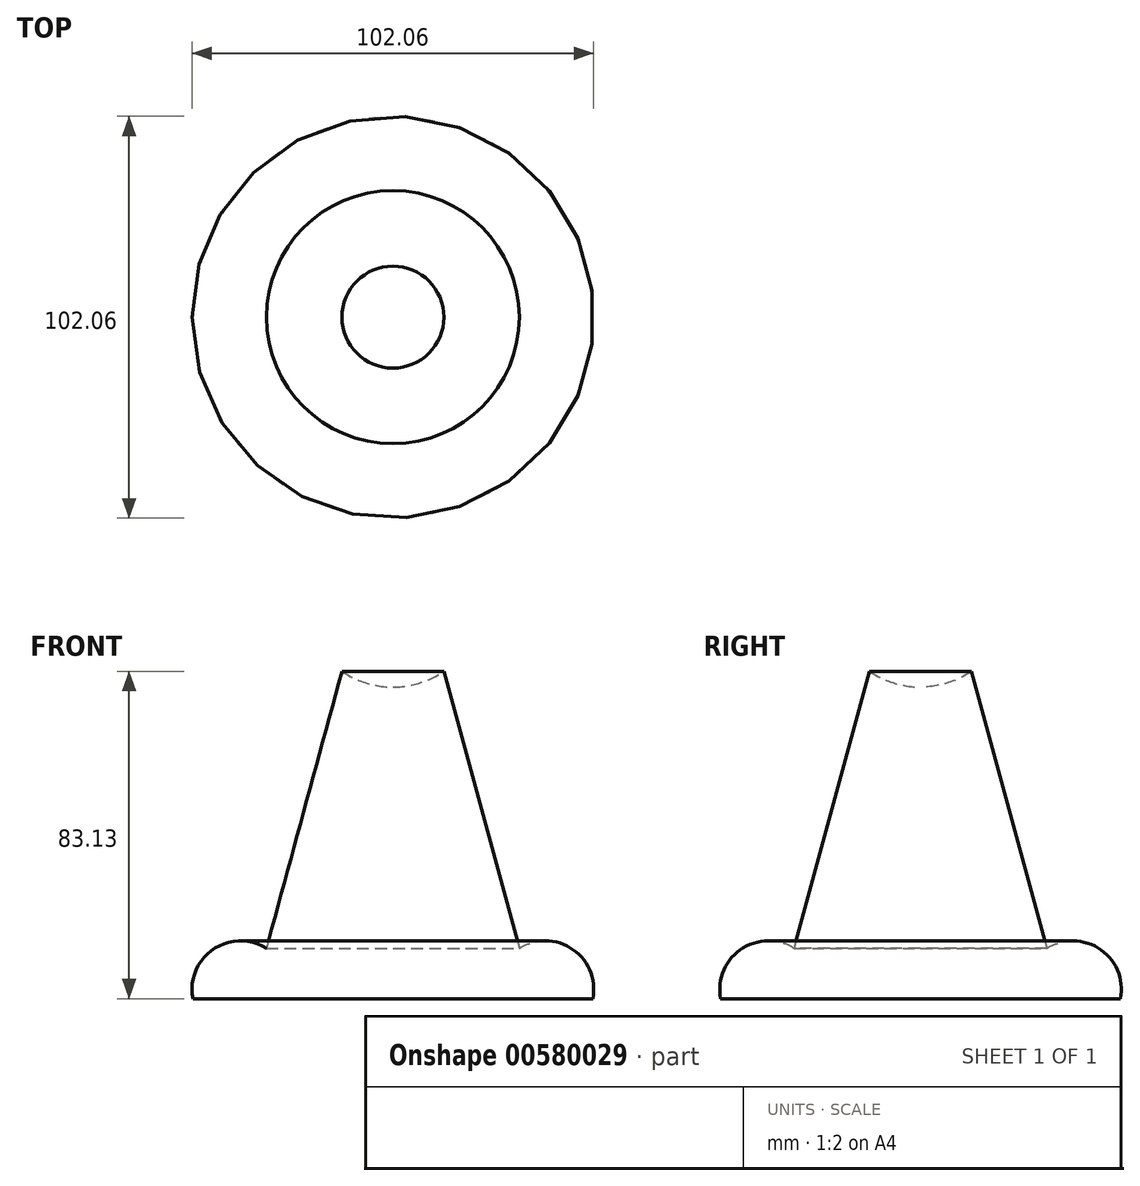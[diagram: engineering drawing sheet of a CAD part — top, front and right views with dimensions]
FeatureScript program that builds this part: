
annotation { "Feature Type Name" : "Feature", "Feature Type Description" : "" }
export const myFeature = defineFeature(function(context is Context, id is Id, definition is map)
    precondition{}
    {
        {
            var Q0;
            Q0=qCreatedBy(makeId("Front.planeOp"),FACE);
            var sketch = newSketch(context, id + "F0", { "sketchPlane" : qUnion([Q0])});
            skLineSegment(sketch, "E0", {"start": v(0, 0) * mm, "end": v(0, 127) * mm});
            skLineSegment(sketch, "E1", {"start": v(0, 0) * mm, "end": v(50.8, 0) * mm});
            skArc(sketch, "E2", {"start": v(50.8, 0) * mm, "mid": v(45.67, 12.54) * mm, "end": v(32.13, 12.8) * mm});
            skLineSegment(sketch, "E3", {"start": v(32.13, 12.8) * mm, "end": v(12.95, 83.13) * mm});
            skArc(sketch, "E4", {"start": v(0, 79.17) * mm, "mid": v(23.69, 103.09) * mm, "end": v(0, 127) * mm});
            skLineSegment(sketch, "E5", {"start": v(32.13, 12.8) * mm, "end": v(0, 12.8) * mm});
            skSolve(sketch);
        }
        {
            var Q0;
            {var subQ0=sQuery(id+"F0.wireOp",EDGE,"E1");Q0=makeQuery(id+"F0.imprint","IMPRINT",FACE,{"disambiguationData":[TD([[makeQuery(id+"F0.imprint","IMPRINT",EDGE,{"derivedFrom":subQ0}),1.0]])]});}
            var Q1;
            {var subQ3=sQuery(id+"F0.wireOp",EDGE,"E5");Q1=makeQuery(id+"F0.imprint","IMPRINT",FACE,{"disambiguationData":[TD([[makeQuery(id+"F0.imprint","IMPRINT",EDGE,{"derivedFrom":subQ3}),-1.0]])]});}
            var Q2;
            {var subQ0=sQuery(id+"F0.wireOp",EDGE,"E4");var subQ1=sQuery(id+"F0.wireOp",EDGE,"E0");var subQ2=makeQuery(id+"F0.imprint","INTERSECT",VERTEX,{"disambiguationData":[OD(0.0)],"derivedFrom":[subQ1,subQ0]});Q2=makeQuery(id+"F0.imprint","IMPRINT",FACE,{"disambiguationData":[TD([[makeQuery(id+"F0.imprint","IMPRINT",EDGE,{"disambiguationData":[TD([[subQ2,1.0]])],"derivedFrom":subQ1}),-1.0]])]});}
            var Q3;
            Q3=sQuery(id+"F0.wireOp",EDGE,"E0");
            revolve(context, id + "F1", {"entities" : qUnion([Q0, Q1, Q2]), "axis" : qUnion([Q3]), "revolveType" : RevolveType.FULL});
        }
    });
